# Revit family: Sink-Kitchen-KOHLER-Vault-K-3935
name_source: partatom
category: Plumbing Fixtures
revit_build: Autodesk Revit 2015 (Build: 20140606_1530(x64)
units: mm (PartAtom-declared; Revit-internal decimal feet)

## types (3) — shared parameters
ADA Compliant = No
Assembly Code = D2010400
CW Connection = No
Cold Water Inlet = Cold Water Inlet
Date Modified = 04/23/2019
Default Elevation = 36"
Description = 29-3/4 inch x 24-5/16 inch x 9-5/16 inch Self-Trimming top-mount single-bowl stainless steel apron-front kitchen sink for 30inch cabinet
Drain Included = No
Finish = Kohler-Metal-NA-Stainless
HW Connection = No
Height = 9 5/16"
Hot Water Inlet = Hot Water Inlet
Length = 29 3/4"
Manufacturer = KOHLER Co.
MasterFormat 1995 = 15410
MasterFormat 2004 = 22.41.16
Material = 18-gauge stainless steel
Product Documentation Link = https://www.us.kohler.com
Product Name = Vault
Product Page URL = http://www.us.kohler.com
URL = https://www.us.kohler.com
Vent Connection = No
Waste Connection = Yes
Waste Water Outlet = Waste Water Outlet
WaterSense Certified = No
Width = 24 5/16"

## per-type parameters (varying)
| type | 3_Hole | 4_Hole | Faucet  Hole Spacing | Fourth Hole Distance | Model | Single Hole | Type |
| Single Hole,NA-Stainless | No | No | 0" | 0" | K-3935-1-NA | Yes | 1 |
| 3 Holes,NA-Stainless | Yes | No | 8" | 0" | K-3935-3-NA | No | 2 |
| 4 Holes,NA-Stainless | No | Yes | 8" | 6 1/8" | K-3935-4-NA | No | 3 |

## geometry (parser evidence)
native form markers: Sweep x6
no freeform markers — native parametric forms only
